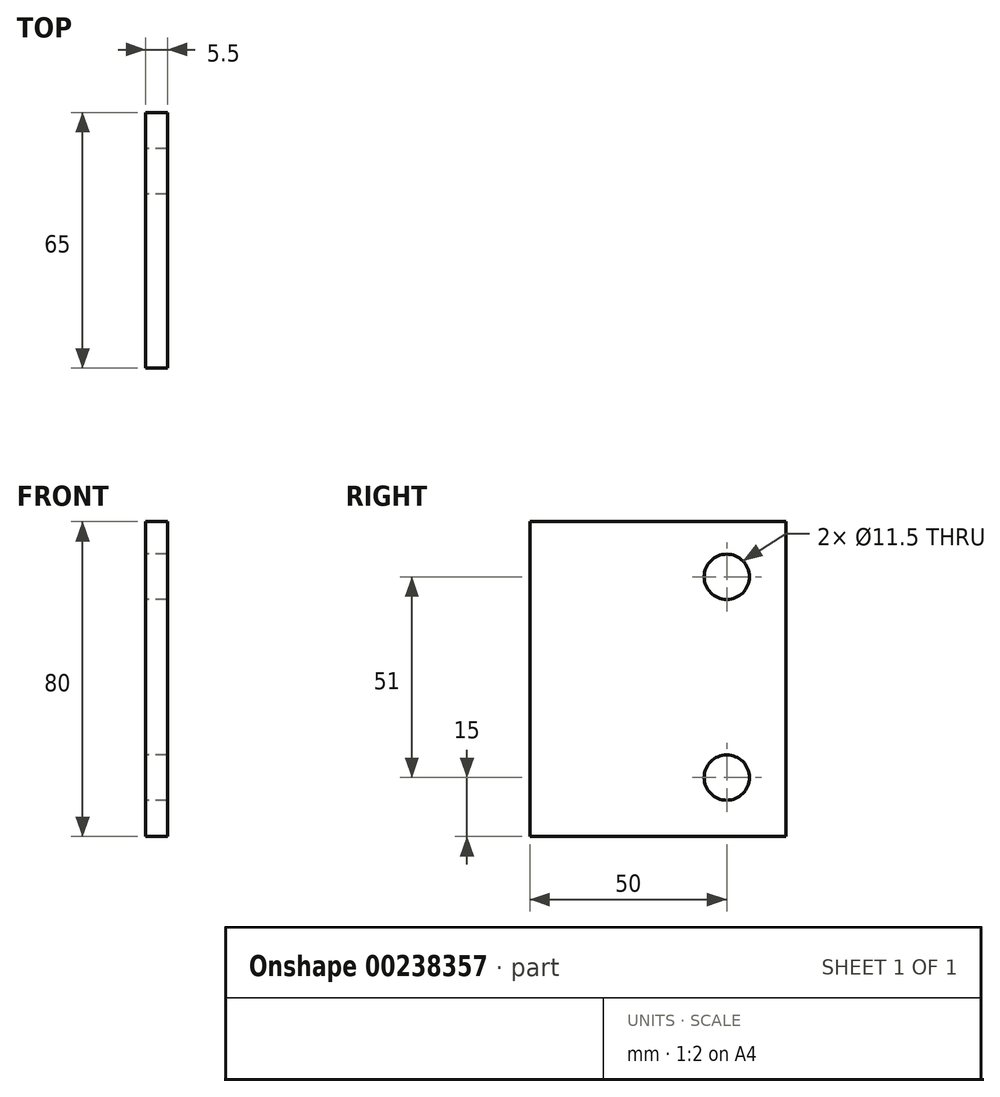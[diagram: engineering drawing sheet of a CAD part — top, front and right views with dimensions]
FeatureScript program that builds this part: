
annotation { "Feature Type Name" : "Feature", "Feature Type Description" : "" }
export const myFeature = defineFeature(function(context is Context, id is Id, definition is map)
    precondition{}
    {
        {
            var Q0;
            Q0=qCreatedBy(makeId("Right.planeOp"),FACE);
            var sketch = newSketch(context, id + "F0", { "sketchPlane" : qUnion([Q0])});
            skLineSegment(sketch, "E0.bottom", {"start": v(32.5, 40) * mm, "end": v(-32.5, 40) * mm});
            skLineSegment(sketch, "E0.top", {"start": v(32.5, -40) * mm, "end": v(-32.5, -40) * mm});
            skLineSegment(sketch, "E0.left", {"start": v(32.5, 40) * mm, "end": v(32.5, -40) * mm});
            skLineSegment(sketch, "E0.right", {"start": v(-32.5, 40) * mm, "end": v(-32.5, -40) * mm});
            skPoint(sketch, "E0.middle", {"position": v(0, 0) * mm});
            skCircle(sketch, "E1", {"center": v(17.5, 26) * mm, "radius": 5.75 * mm});
            skCircle(sketch, "E2", {"center": v(17.5, -25) * mm, "radius": 5.75 * mm});
            skLineSegment(sketch, "E3", {"start": v(17.5, 26) * mm, "end": v(17.5, -25) * mm, "construction": true});
            skSolve(sketch);
        }
        {
            var Q0;
            Q0 = qSketchRegion(id + "F0", true);
            extrude(context, id + "F1", {"entities" : qUnion([Q0]), "depth" : 5.5 * mm});
        }
    });
